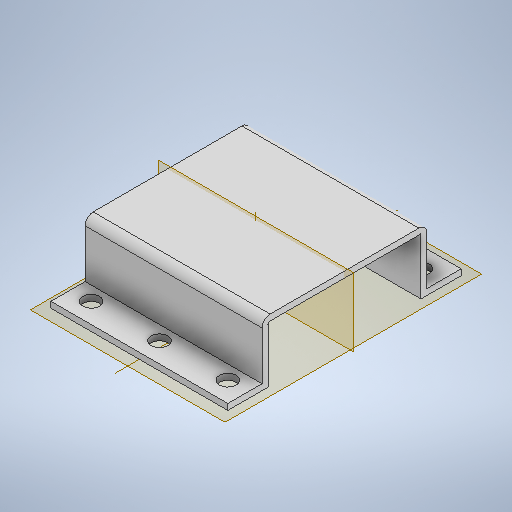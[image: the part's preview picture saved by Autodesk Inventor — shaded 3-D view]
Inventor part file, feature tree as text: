
AUTODESK INVENTOR PART (.ipt)
format: ipt  version: 2025 (Build 290162000, 162)  size: 265,728 bytes
history: native  units: mm
features: sketch x2, extrude x1, hole x1, mirror x1
ambient origin geometry x8: Origin, YZ Plane, XZ Plane, XY Plane, X Axis, Y Axis, Z Axis, Center Point
bodies: Solid1 (feature_tree)
feature tree (5):
  extrude  "Extrusion1"  Depth=1.5mm
  hole  "Hole1"  [1 undecoded]
  mirror  "Mirror1"
  sketch  "Sketch2"  dims[d0=10.0mm d1=1.5mm]
  sketch  "Sketch3"  dims[d2=8.5mm d4=14.0mm d5=19.0mm d6=1.5mm d7=2.0mm d8=44.0mm d9=0.0mm d10=5.0mm d12=17.0mm d14=5.0mm d15=4.2mm d16=6.0mm d17=4.0mm d18=2.0mm d19=90.0deg d20=8.0mm d21=20.594885mm d22=0.5mm d23=17.0mm d24=5.0mm]
note: 1 required parameter value undecoded (feature->parameter linkage not recoverable at this tier; creation-order binding heuristic only, values carry confidence <= 0.55)
